# Revit family: Fluorescent Recesses Lighting Fixture
name_source: partatom
category: Lighting Fixtures
revit_build: Autodesk Revit 2015 (Build: 20141119_0715(x64)
units: mm (PartAtom-declared; Revit-internal decimal feet)

## types (6) — shared parameters
Color Filter = 16777215
Default Elevation = 4' - 0"
Depth = 0' - 6"
Dimming Lamp Color Temperature Shift = <None>
Emit Shape Visible in Rendering = No
Lamp = LAMP TYPE
Manufacturer = MANUFACTURER
Tilt Angle = -90.00°
Type Comments = REMARKS
Wattage Comments = #LAMPS

## per-type parameters (varying)
| type | Apparent Load | Description | Emergency Load | Emergency Voltage | Emit from Rectangle Length | Emit from Rectangle Width | Length | Normal Voltage | Photometric Web File | Width |
| 1x4 - 120 | 64 VA | DESCRIPTION | 32 VA | 120 V | 4' - 0" | 1' - 0" | 4' - 0" | 120 V | 1x42A12.ies | 1' - 0" |
| 1x4 - 277 | 64 VA | DESCRIPTION | 32 VA | 277 V | 4' - 0" | 1' - 0" | 4' - 0" | 277 V | 1x42A12.ies | 1' - 0" |
| 2x2 - 120 | 62 VA | DESCRIPTION | 31 VA | 120 V | 2' - 0" | 2' - 0" | 2' - 0" | 120 V | 2x22UA12.ies | 2' - 0" |
| 2x2 - 277 | 31 VA | DESCRIPTION | 31 VA | 277 V | 2' - 0" | 2' - 0" | 2' - 0" | 277 V | 2x22UA12.ies | 2' - 0" |
| 2x4 - 120 | 96 VA | DESCRIPTION | 32 VA | 120 V | 4' - 0" | 2' - 0" | 4' - 0" | 120 V | 2x43A12.ies | 2' - 0" |
| 2x4 - 277 | 96 VA |  | 32 VA | 120 V | 4' - 0" | 2' - 0" | 4' - 0" | 277 V | 2x43A12.ies | 2' - 0" |

## geometry (parser evidence)
native form markers: Sweep x3
no freeform markers — native parametric forms only
